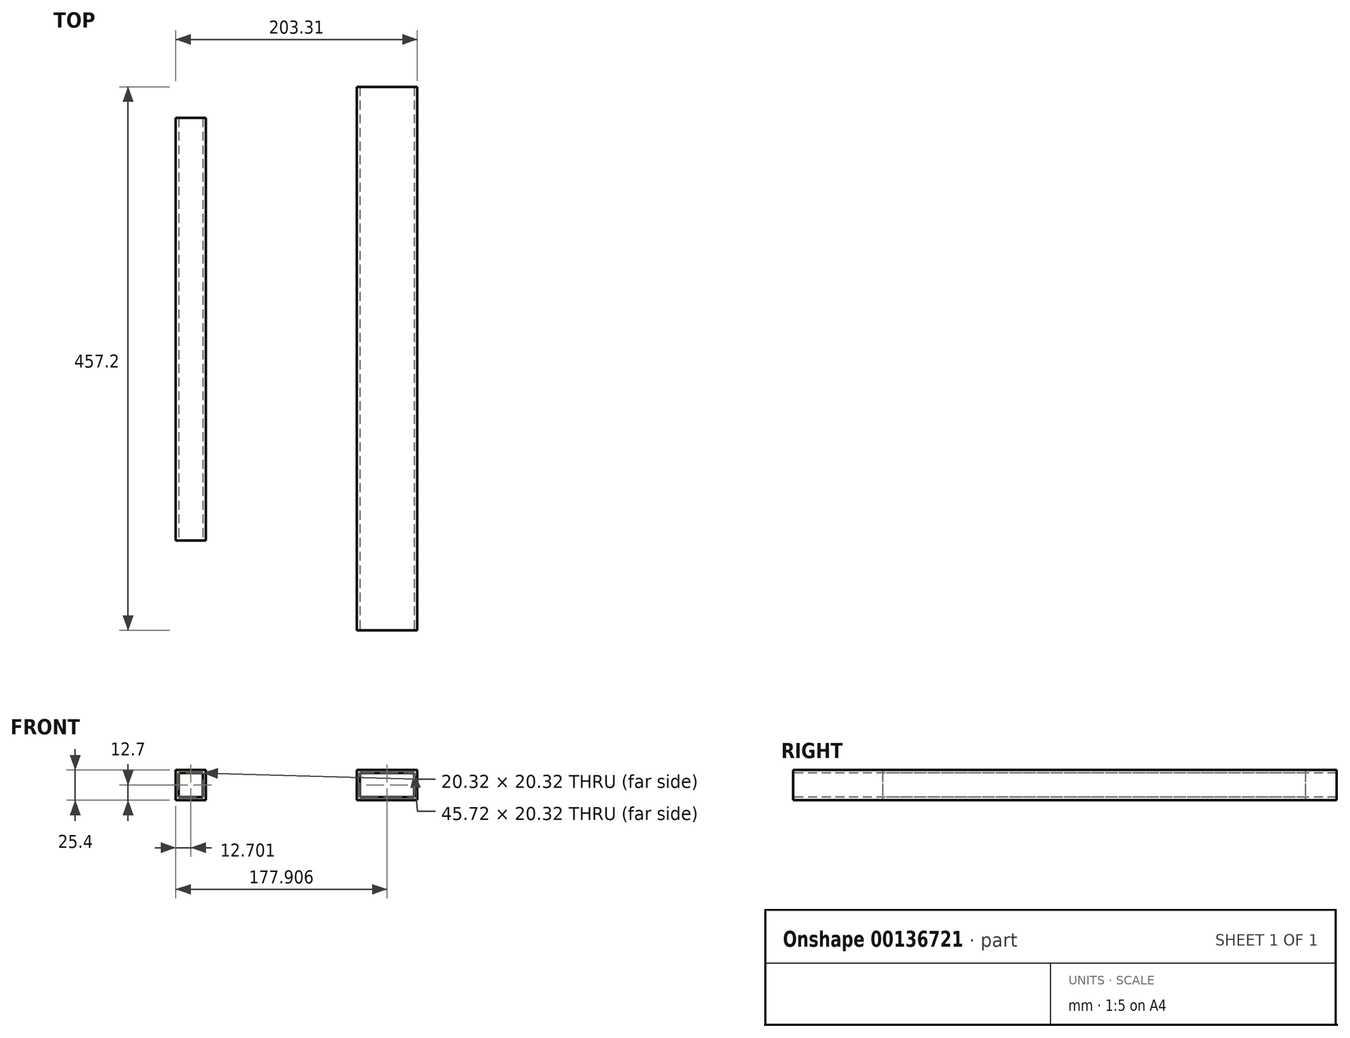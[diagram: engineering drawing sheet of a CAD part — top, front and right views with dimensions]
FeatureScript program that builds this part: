
annotation { "Feature Type Name" : "Feature", "Feature Type Description" : "" }
export const myFeature = defineFeature(function(context is Context, id is Id, definition is map)
    precondition{}
    {
        {
            var Q0;
            Q0=qCreatedBy(makeId("Top.planeOp"),FACE);
            var sketch = newSketch(context, id + "F0", { "sketchPlane" : qUnion([Q0])});
            skLineSegment(sketch, "E0.bottom", {"start": v(-14.11, 218.72) * mm, "end": v(36.69, 218.72) * mm});
            skLineSegment(sketch, "E0.top", {"start": v(-14.11, -238.48) * mm, "end": v(36.69, -238.48) * mm});
            skLineSegment(sketch, "E0.left", {"start": v(-14.11, 218.72) * mm, "end": v(-14.11, -238.48) * mm});
            skLineSegment(sketch, "E0.right", {"start": v(36.69, 218.72) * mm, "end": v(36.69, -238.48) * mm});
            skSolve(sketch);
        }
        {
            var Q0;
            Q0 = qSketchRegion(id + "F0", true);
            extrude(context, id + "F1", {"entities" : qUnion([Q0]), "endBound" : BoundingType.SYMMETRIC, "depth" : 25.4 * mm});
        }
        {
            var Q0;
            Q0=makeQuery(id+"F1.opExtrude","SWEPT_FACE",FACE,{"disambiguationData":[OSD([sQuery(id+"F0.wireOp",EDGE,"E0.bottom")])]});
            var Q1;
            Q1=makeQuery(id+"F1.opExtrude","SWEPT_FACE",FACE,{"disambiguationData":[OSD([sQuery(id+"F0.wireOp",EDGE,"E0.top")])]});
            shell(context, id + "F2", {"entities" : qUnion([Q0, Q1]), "thickness" : 2.54 * mm});
        }
        {
            var Q0;
            Q0=qCreatedBy(makeId("Top.planeOp"),FACE);
            var sketch = newSketch(context, id + "F3", { "sketchPlane" : qUnion([Q0])});
            skLineSegment(sketch, "E1.bottom", {"start": v(-166.62, 192.58) * mm, "end": v(-141.22, 192.58) * mm});
            skLineSegment(sketch, "E1.top", {"start": v(-166.62, -163.02) * mm, "end": v(-141.22, -163.02) * mm});
            skLineSegment(sketch, "E1.left", {"start": v(-166.62, 192.58) * mm, "end": v(-166.62, -163.02) * mm});
            skLineSegment(sketch, "E1.right", {"start": v(-141.22, 192.58) * mm, "end": v(-141.22, -163.02) * mm});
            skSolve(sketch);
        }
        {
            var Q0;
            Q0 = qSketchRegion(id + "F3", true);
            extrude(context, id + "F4", {"entities" : qUnion([Q0]), "endBound" : BoundingType.SYMMETRIC, "depth" : 25.4 * mm});
        }
        {
            var Q0;
            Q0=makeQuery(id+"F4.opExtrude","SWEPT_FACE",FACE,{"disambiguationData":[OSD([sQuery(id+"F3.wireOp",EDGE,"E1.bottom")])]});
            var Q1;
            Q1=makeQuery(id+"F4.opExtrude","SWEPT_FACE",FACE,{"disambiguationData":[OSD([sQuery(id+"F3.wireOp",EDGE,"E1.top")])]});
            shell(context, id + "F5", {"entities" : qUnion([Q0, Q1]), "thickness" : 2.54 * mm});
        }
    });
